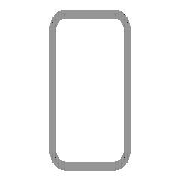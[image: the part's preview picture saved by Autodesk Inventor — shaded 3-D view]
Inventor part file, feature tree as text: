
AUTODESK INVENTOR PART (.ipt)
format: ipt  version: 2025 (Build 290162010, 162A)  size: 133,632 bytes
history: native  units: mm (DEFAULTED — no unit token found)
features: other x4, sketch x1, plane x1
ambient origin geometry x8: Origin, YZ Plane, XZ Plane, XY Plane, X Axis, Y Axis, Z Axis, Center Point
bodies: Solid1 (feature_tree), Body (feature_tree)
feature tree (6):
  parser-record x1  (decoder bookkeeping rows leaked as tree rows — omitted from the tree; the rows remain in map.json)
  other  "Driven Length"
  other  "Start Plane"
  other  "End Plane"
  sketch  "Sketch3"  dims[d3=2382.0mm d4=0.0mm d7=4.0mm d9=40.0mm d11=80.0mm d12=2.0mm d13=-0.0mm d14=2382.0mm d15=20.0mm d16=40.0mm d17=90.0deg d18=2382.0mm]
  plane  "Work Plane3"
